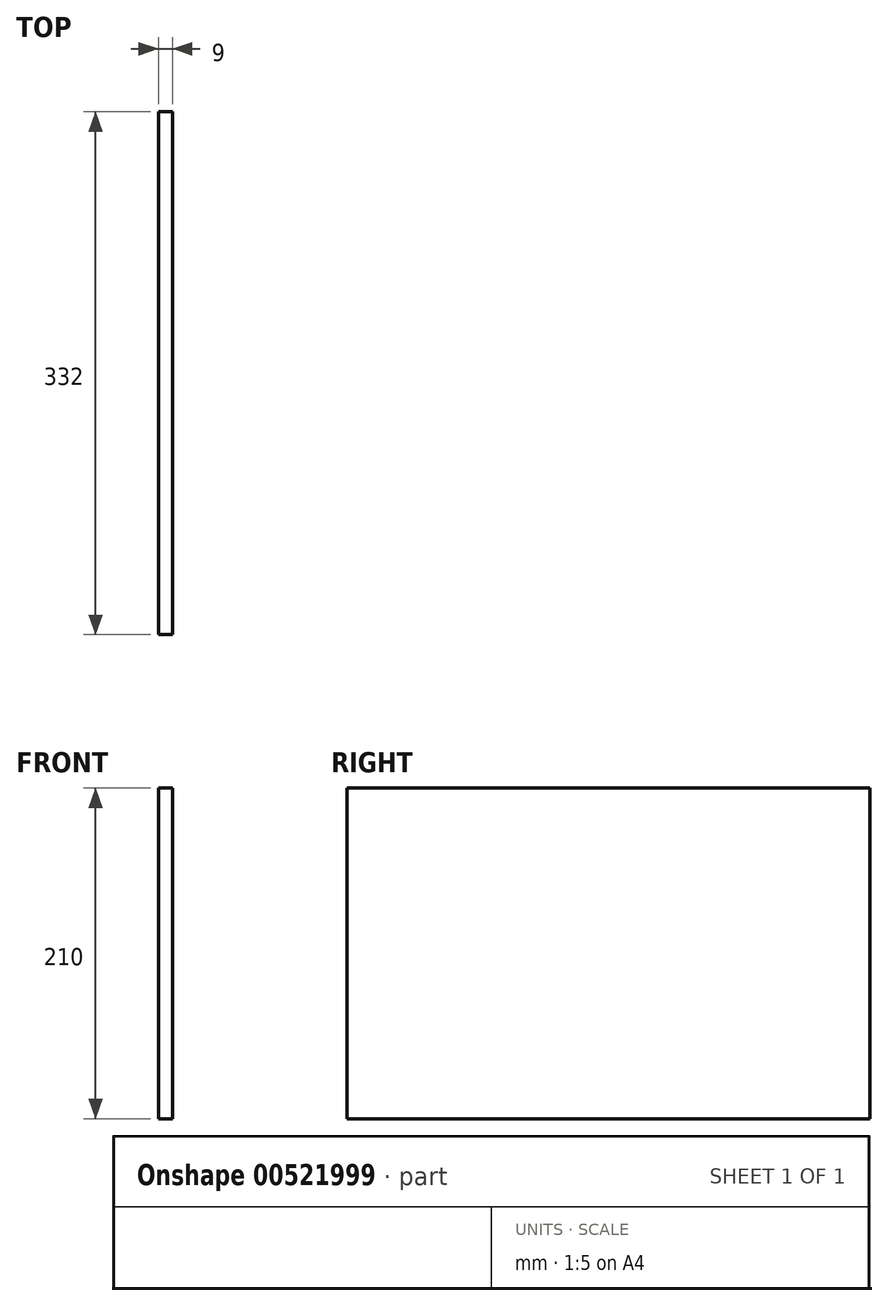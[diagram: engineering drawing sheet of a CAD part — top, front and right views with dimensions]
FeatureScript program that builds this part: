
annotation { "Feature Type Name" : "Feature", "Feature Type Description" : "" }
export const myFeature = defineFeature(function(context is Context, id is Id, definition is map)
    precondition{}
    {
        {
            var Q0;
            Q0=qCreatedBy(makeId("Right.planeOp"),FACE);
            var sketch = newSketch(context, id + "F0", { "sketchPlane" : qUnion([Q0])});
            skLineSegment(sketch, "E0.bottom", {"start": v(0, 0) * mm, "end": v(-332, 0) * mm});
            skLineSegment(sketch, "E0.top", {"start": v(0, 210) * mm, "end": v(-332, 210) * mm});
            skLineSegment(sketch, "E0.left", {"start": v(0, 0) * mm, "end": v(0, 210) * mm});
            skLineSegment(sketch, "E0.right", {"start": v(-332, 0) * mm, "end": v(-332, 210) * mm});
            skSolve(sketch);
        }
        {
            var Q0;
            Q0=makeQuery(id+"F0.imprint","IMPRINT",FACE,{"disambiguationData":[TD([[makeQuery(id+"F0.imprint","IMPRINT",EDGE,{"derivedFrom":sQuery(id+"F0.wireOp",EDGE,"E0.bottom")}),-1.0]])]});
            extrude(context, id + "F1", {"entities" : qUnion([Q0]), "depth" : 9 * mm, "offsetDistance" : 25 * mm});
        }
    });
